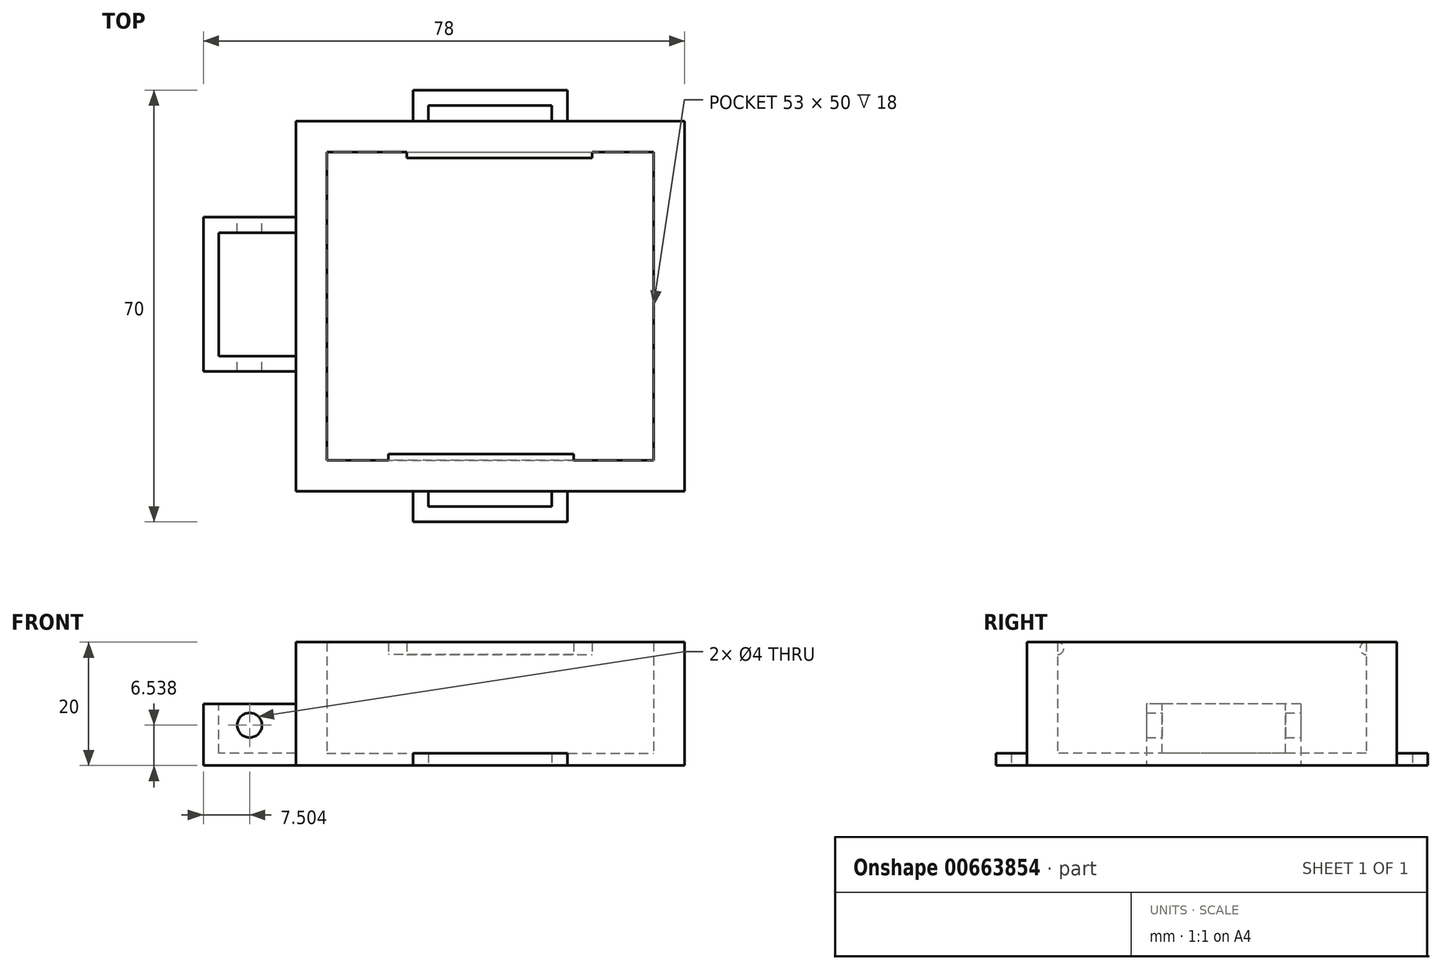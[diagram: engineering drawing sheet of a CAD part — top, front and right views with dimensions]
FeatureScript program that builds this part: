
annotation { "Feature Type Name" : "Feature", "Feature Type Description" : "" }
export const myFeature = defineFeature(function(context is Context, id is Id, definition is map)
    precondition{}
    {
        {
            var Q0;
            Q0=qCreatedBy(makeId("Top.planeOp"),FACE);
            var sketch = newSketch(context, id + "F0", { "sketchPlane" : qUnion([Q0])});
            skLineSegment(sketch, "E0.bottom", {"start": v(-6.99, 15.58) * mm, "end": v(46.01, 15.58) * mm});
            skLineSegment(sketch, "E0.top", {"start": v(-6.99, -34.42) * mm, "end": v(46.01, -34.42) * mm});
            skLineSegment(sketch, "E0.left", {"start": v(-6.99, 15.58) * mm, "end": v(-6.99, -34.42) * mm});
            skLineSegment(sketch, "E0.right", {"start": v(46.01, 15.58) * mm, "end": v(46.01, -34.42) * mm});
            skLineSegment(sketch, "E1.bottom", {"start": v(-11.99, 20.58) * mm, "end": v(51.01, 20.58) * mm});
            skLineSegment(sketch, "E1.top", {"start": v(-11.99, -39.42) * mm, "end": v(51.01, -39.42) * mm});
            skLineSegment(sketch, "E1.left", {"start": v(-11.99, 20.58) * mm, "end": v(-11.99, -39.42) * mm});
            skLineSegment(sketch, "E1.right", {"start": v(51.01, 20.58) * mm, "end": v(51.01, -39.42) * mm});
            skSolve(sketch);
        }
        {
            var Q0;
            Q0 = qSketchRegion(id + "F0", true);
            extrude(context, id + "F1", {"entities" : qUnion([Q0]), "depth" : 20 * mm, "offsetDistance" : 25 * mm});
        }
        {
            var Q0;
            Q0=qCreatedBy(makeId("Top.planeOp"),FACE);
            var sketch = newSketch(context, id + "F2", { "sketchPlane" : qUnion([Q0])});
            skLineSegment(sketch, "E2.bottom", {"start": v(7.01, 20.58) * mm, "end": v(32.01, 20.58) * mm});
            skLineSegment(sketch, "E2.top", {"start": v(7.01, 25.58) * mm, "end": v(32.01, 25.58) * mm});
            skLineSegment(sketch, "E2.left", {"start": v(7.01, 20.58) * mm, "end": v(7.01, 25.58) * mm});
            skLineSegment(sketch, "E2.right", {"start": v(32.01, 20.58) * mm, "end": v(32.01, 25.58) * mm});
            skLineSegment(sketch, "E3.bottom", {"start": v(7.01, -39.42) * mm, "end": v(32.01, -39.42) * mm});
            skLineSegment(sketch, "E3.top", {"start": v(7.01, -44.42) * mm, "end": v(32.01, -44.42) * mm});
            skLineSegment(sketch, "E3.left", {"start": v(7.01, -39.42) * mm, "end": v(7.01, -44.42) * mm});
            skLineSegment(sketch, "E3.right", {"start": v(32.01, -39.42) * mm, "end": v(32.01, -44.42) * mm});
            skLineSegment(sketch, "E4.bottom", {"start": v(9.51, -39.42) * mm, "end": v(29.51, -39.42) * mm});
            skLineSegment(sketch, "E4.top", {"start": v(9.51, -41.92) * mm, "end": v(29.51, -41.92) * mm});
            skLineSegment(sketch, "E4.left", {"start": v(9.51, -39.42) * mm, "end": v(9.51, -41.92) * mm});
            skLineSegment(sketch, "E4.right", {"start": v(29.51, -39.42) * mm, "end": v(29.51, -41.92) * mm});
            skLineSegment(sketch, "E5.bottom", {"start": v(9.51, 20.58) * mm, "end": v(29.51, 20.58) * mm});
            skLineSegment(sketch, "E5.top", {"start": v(9.51, 23.08) * mm, "end": v(29.51, 23.08) * mm});
            skLineSegment(sketch, "E5.left", {"start": v(9.51, 20.58) * mm, "end": v(9.51, 23.08) * mm});
            skLineSegment(sketch, "E5.right", {"start": v(29.51, 20.58) * mm, "end": v(29.51, 23.08) * mm});
            skSolve(sketch);
        }
        {
            var Q0;
            Q0=makeQuery(id+"F2.imprint","IMPRINT",FACE,{"disambiguationData":[TD([[makeQuery(id+"F2.imprint","IMPRINT",EDGE,{"derivedFrom":sQuery(id+"F2.wireOp",EDGE,"E2.top")}),-1.0]])]});
            var Q1;
            Q1=makeQuery(id+"F2.imprint","IMPRINT",FACE,{"disambiguationData":[TD([[makeQuery(id+"F2.imprint","IMPRINT",EDGE,{"derivedFrom":sQuery(id+"F2.wireOp",EDGE,"E3.top")}),1.0]])]});
            extrude(context, id + "F3", {"entities" : qUnion([Q0, Q1]), "operationType" : NewBodyOperationType.ADD, "depth" : 2 * mm, "offsetDistance" : 25 * mm});
        }
        {
            var Q0;
            Q0=makeQuery(id+"F0.imprint","IMPRINT",FACE,{"disambiguationData":[TD([[makeQuery(id+"F0.imprint","IMPRINT",EDGE,{"derivedFrom":sQuery(id+"F0.wireOp",EDGE,"E0.bottom")}),-1.0]])]});
            extrude(context, id + "F4", {"entities" : qUnion([Q0]), "operationType" : NewBodyOperationType.ADD, "depth" : 2 * mm, "offsetDistance" : 25 * mm});
        }
        {
            var Q0;
            Q0=makeQuery(id+"F1.opExtrude","SWEPT_FACE",FACE,{"disambiguationData":[OSD([sQuery(id+"F0.wireOp",EDGE,"E0.bottom")])]});
            var sketch = newSketch(context, id + "F5", { "sketchPlane" : qUnion([Q0])});
            skLineSegment(sketch, "E6.bottom", {"start": v(6.01, 20) * mm, "end": v(36.01, 20) * mm});
            skLineSegment(sketch, "E6.top", {"start": v(6.01, 18) * mm, "end": v(36.01, 18) * mm});
            skLineSegment(sketch, "E6.left", {"start": v(6.01, 20) * mm, "end": v(6.01, 18) * mm});
            skLineSegment(sketch, "E6.right", {"start": v(36.01, 20) * mm, "end": v(36.01, 18) * mm});
            skSolve(sketch);
        }
        {
            var Q0;
            Q0 = qSketchRegion(id + "F5", true);
            extrude(context, id + "F6", {"entities" : qUnion([Q0]), "operationType" : NewBodyOperationType.ADD, "depth" : 1 * mm, "offsetDistance" : 25 * mm});
        }
        {
            var Q0;
            Q0=makeQuery(id+"F1.opExtrude","SWEPT_FACE",FACE,{"disambiguationData":[OSD([sQuery(id+"F0.wireOp",EDGE,"E0.top")])]});
            var sketch = newSketch(context, id + "F7", { "sketchPlane" : qUnion([Q0])});
            skLineSegment(sketch, "E7.bottom", {"start": v(-33.01, 20) * mm, "end": v(-3.01, 20) * mm});
            skLineSegment(sketch, "E7.top", {"start": v(-33.01, 18) * mm, "end": v(-3.01, 18) * mm});
            skLineSegment(sketch, "E7.left", {"start": v(-33.01, 20) * mm, "end": v(-33.01, 18) * mm});
            skLineSegment(sketch, "E7.right", {"start": v(-3.01, 20) * mm, "end": v(-3.01, 18) * mm});
            skSolve(sketch);
        }
        {
            var Q0;
            Q0 = qSketchRegion(id + "F7", true);
            extrude(context, id + "F8", {"entities" : qUnion([Q0]), "operationType" : NewBodyOperationType.ADD, "depth" : 1 * mm, "offsetDistance" : 25 * mm});
        }
        {
            var Q0;
            Q0=makeQuery(id+"F6.opExtrude","CAP_EDGE",EDGE,{"disambiguationData":[OSD([sQuery(id+"F5.wireOp",EDGE,"E6.bottom")])],"isStart":false});
            var Q1;
            Q1=makeQuery(id+"F6.opExtrude","CAP_EDGE",EDGE,{"disambiguationData":[OSD([sQuery(id+"F5.wireOp",EDGE,"E6.top")])],"isStart":false});
            var Q2;
            Q2=makeQuery(id+"F8.opExtrude","CAP_EDGE",EDGE,{"disambiguationData":[OSD([sQuery(id+"F7.wireOp",EDGE,"E7.bottom")])],"isStart":false});
            var Q3;
            Q3=makeQuery(id+"F8.opExtrude","CAP_EDGE",EDGE,{"disambiguationData":[OSD([sQuery(id+"F7.wireOp",EDGE,"E7.top")])],"isStart":false});
            fillet(context, id + "F9", {"entities" : qUnion([Q0, Q1, Q2, Q3]), "radius" : 1 * mm, "tangentPropagation" : true, "allowEdgeOverflow" : false});
        }
        {
            var Q0;
            Q0=qCreatedBy(makeId("Top.planeOp"),FACE);
            var sketch = newSketch(context, id + "F10", { "sketchPlane" : qUnion([Q0])});
            skLineSegment(sketch, "E8.bottom", {"start": v(-11.99, 5) * mm, "end": v(-26.99, 5) * mm});
            skLineSegment(sketch, "E8.top", {"start": v(-11.99, -20) * mm, "end": v(-26.99, -20) * mm});
            skLineSegment(sketch, "E8.left", {"start": v(-11.99, 5) * mm, "end": v(-11.99, -20) * mm});
            skLineSegment(sketch, "E8.right", {"start": v(-26.99, 5) * mm, "end": v(-26.99, -20) * mm});
            skSolve(sketch);
        }
        {
            var Q0;
            Q0 = qSketchRegion(id + "F10", true);
            extrude(context, id + "F11", {"entities" : qUnion([Q0]), "operationType" : NewBodyOperationType.ADD, "depth" : 10 * mm, "offsetDistance" : 25 * mm});
        }
        {
            var Q0;
            Q0=makeQuery(id+"F11.opExtrude","CAP_FACE",FACE,{"disambiguationData":[OSD([sQuery(id+"F10.wireOp",EDGE,"E8.bottom"),sQuery(id+"F10.wireOp",EDGE,"E8.top"),sQuery(id+"F10.wireOp",EDGE,"E8.left"),sQuery(id+"F10.wireOp",EDGE,"E8.right")])],"isStart":false});
            var sketch = newSketch(context, id + "F12", { "sketchPlane" : qUnion([Q0])});
            skLineSegment(sketch, "E9.bottom", {"start": v(-11.99, 2.5) * mm, "end": v(-24.49, 2.5) * mm});
            skLineSegment(sketch, "E9.top", {"start": v(-11.99, -17.5) * mm, "end": v(-24.49, -17.5) * mm});
            skLineSegment(sketch, "E9.left", {"start": v(-11.99, 2.5) * mm, "end": v(-11.99, -17.5) * mm});
            skLineSegment(sketch, "E9.right", {"start": v(-24.49, 2.5) * mm, "end": v(-24.49, -17.5) * mm});
            skSolve(sketch);
        }
        {
            var Q0;
            Q0 = qSketchRegion(id + "F12", true);
            extrude(context, id + "F13", {"entities" : qUnion([Q0]), "operationType" : NewBodyOperationType.REMOVE, "oppositeDirection" : true, "depth" : 8 * mm, "offsetDistance" : 25 * mm});
        }
        {
            var Q0;
            Q0=makeQuery(id+"F11.opExtrude","SWEPT_FACE",FACE,{"disambiguationData":[OSD([sQuery(id+"F10.wireOp",EDGE,"E8.bottom")])]});
            var sketch = newSketch(context, id + "F14", { "sketchPlane" : qUnion([Q0])});
            skCircle(sketch, "E10", {"center": v(19.49, 6.54) * mm, "radius": 2 * mm});
            skPoint(sketch, "E10.centerSnap0", {"position": v(19.49, 0) * mm});
            skSolve(sketch);
        }
        {
            var Q0;
            Q0 = qSketchRegion(id + "F14", true);
            extrude(context, id + "F15", {"entities" : qUnion([Q0]), "operationType" : NewBodyOperationType.REMOVE, "oppositeDirection" : true, "depth" : 25 * mm, "offsetDistance" : 25 * mm});
        }
    });
